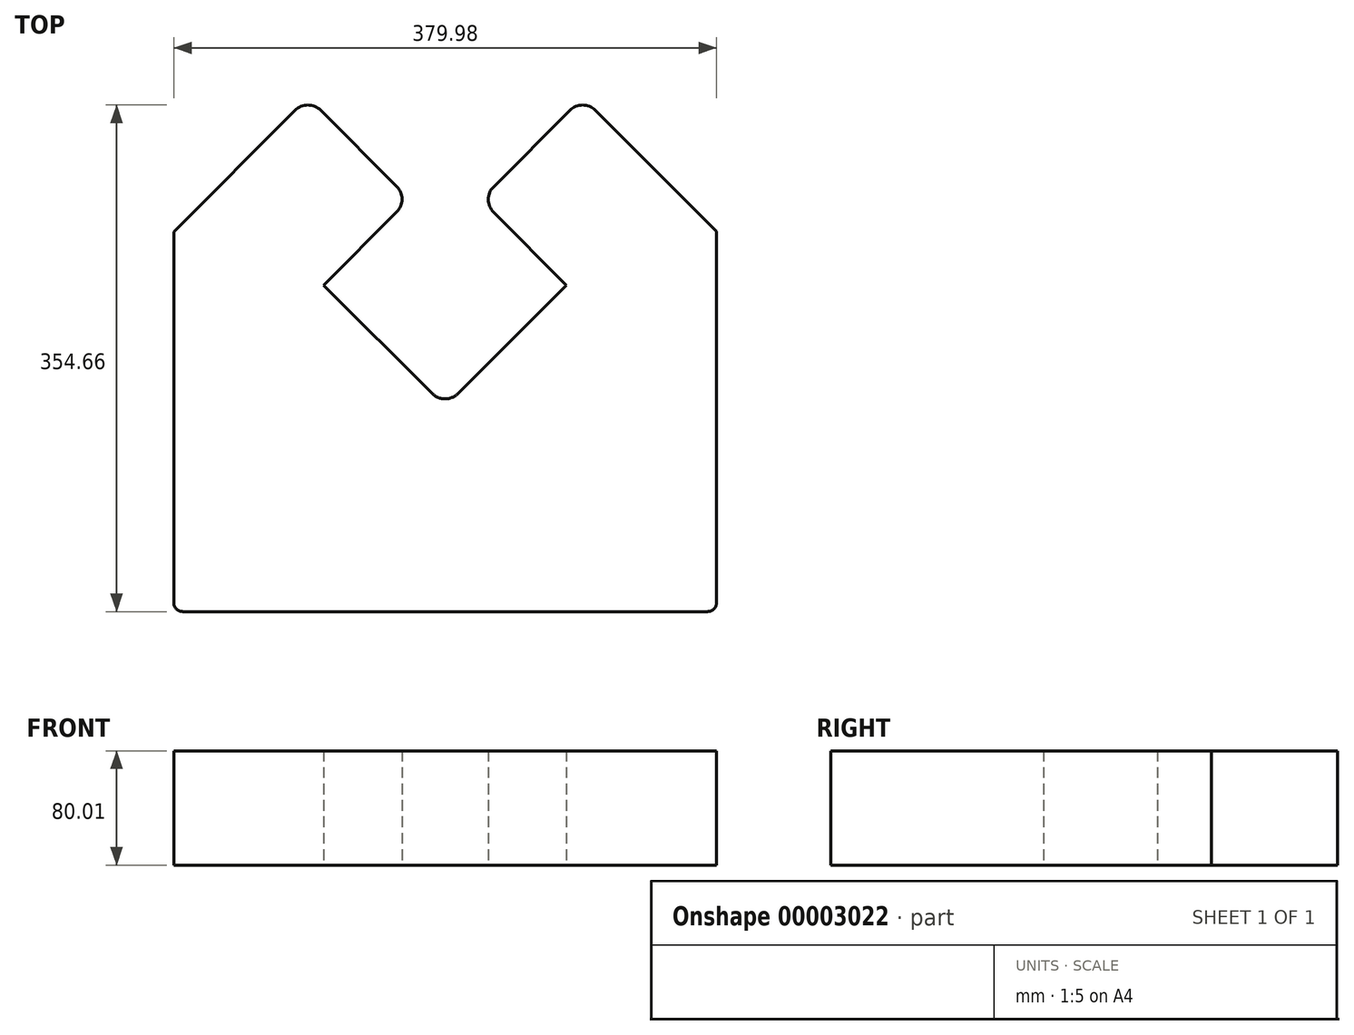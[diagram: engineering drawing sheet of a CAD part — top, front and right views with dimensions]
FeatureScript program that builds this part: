
annotation { "Feature Type Name" : "Feature", "Feature Type Description" : "" }
export const myFeature = defineFeature(function(context is Context, id is Id, definition is map)
    precondition{}
    {
        {
            var Q0;
            Q0=qCreatedBy(makeId("Top.planeOp"),FACE);
            var sketch = newSketch(context, id + "F0", { "sketchPlane" : qUnion([Q0])});
            skLineSegment(sketch, "E0", {"start": v(6.35, 0) * mm, "end": v(373.63, 0) * mm});
            skLineSegment(sketch, "E1", {"start": v(379.98, 6.35) * mm, "end": v(379.98, 266.25) * mm});
            skLineSegment(sketch, "E2", {"start": v(379.98, 266.25) * mm, "end": v(295.2, 350.94) * mm});
            skLineSegment(sketch, "E3", {"start": v(277.25, 350.93) * mm, "end": v(223.86, 297.5) * mm});
            skLineSegment(sketch, "E4", {"start": v(223.87, 279.54) * mm, "end": v(274.85, 228.6) * mm});
            skLineSegment(sketch, "E5", {"start": v(274.85, 228.6) * mm, "end": v(198.97, 152.64) * mm});
            skLineSegment(sketch, "E6", {"start": v(181, 152.63) * mm, "end": v(104.97, 228.6) * mm});
            skLineSegment(sketch, "E7", {"start": v(104.97, 228.6) * mm, "end": v(156.12, 279.8) * mm});
            skLineSegment(sketch, "E8", {"start": v(156.12, 297.77) * mm, "end": v(102.9, 350.94) * mm});
            skLineSegment(sketch, "E9", {"start": v(84.93, 350.93) * mm, "end": v(0, 265.92) * mm});
            skLineSegment(sketch, "E10", {"start": v(0, 265.92) * mm, "end": v(0, 6.35) * mm});
            skPoint(sketch, "E11.visualSharp", {"position": v(0, 0) * mm});
            skArc(sketch, "E11.filletArc", {"start": v(0, 6.35) * mm, "mid": v(1.86, 1.86) * mm, "end": v(6.35, 0) * mm});
            skPoint(sketch, "E12.visualSharp", {"position": v(379.98, 0) * mm});
            skArc(sketch, "E12.filletArc", {"start": v(373.63, 0) * mm, "mid": v(378.12, 1.86) * mm, "end": v(379.98, 6.35) * mm});
            skPoint(sketch, "E13.visualSharp", {"position": v(190, 143.66) * mm});
            skPoint(sketch, "E14.visualSharp", {"position": v(93.9, 359.92) * mm});
            skArc(sketch, "E14.filletArc", {"start": v(102.9, 350.94) * mm, "mid": v(93.9, 354.66) * mm, "end": v(84.93, 350.93) * mm});
            skPoint(sketch, "E15.visualSharp", {"position": v(286.22, 359.92) * mm});
            skArc(sketch, "E15.filletArc", {"start": v(295.2, 350.94) * mm, "mid": v(286.22, 354.66) * mm, "end": v(277.25, 350.93) * mm});
            skPoint(sketch, "E16.visualSharp", {"position": v(214.88, 288.51) * mm});
            skArc(sketch, "E16.filletArc", {"start": v(223.86, 297.5) * mm, "mid": v(220.14, 288.51) * mm, "end": v(223.87, 279.54) * mm});
            skPoint(sketch, "E17.visualSharp", {"position": v(165.1, 288.8) * mm});
            skArc(sketch, "E17.filletArc", {"start": v(156.12, 279.8) * mm, "mid": v(159.84, 288.8) * mm, "end": v(156.12, 297.77) * mm});
            skArc(sketch, "E18.filletArc", {"start": v(181, 152.63) * mm, "mid": v(189.99, 148.92) * mm, "end": v(198.97, 152.64) * mm});
            skSolve(sketch);
        }
        {
            var Q0;
            Q0=makeQuery(id+"F0.imprint","IMPRINT",FACE,{"disambiguationData":[TD([[makeQuery(id+"F0.imprint","IMPRINT",EDGE,{"derivedFrom":sQuery(id+"F0.wireOp",EDGE,"E0")}),1.0]])]});
            extrude(context, id + "F1", {"entities" : qUnion([Q0]), "depth" : 80 * mm});
        }
    });
